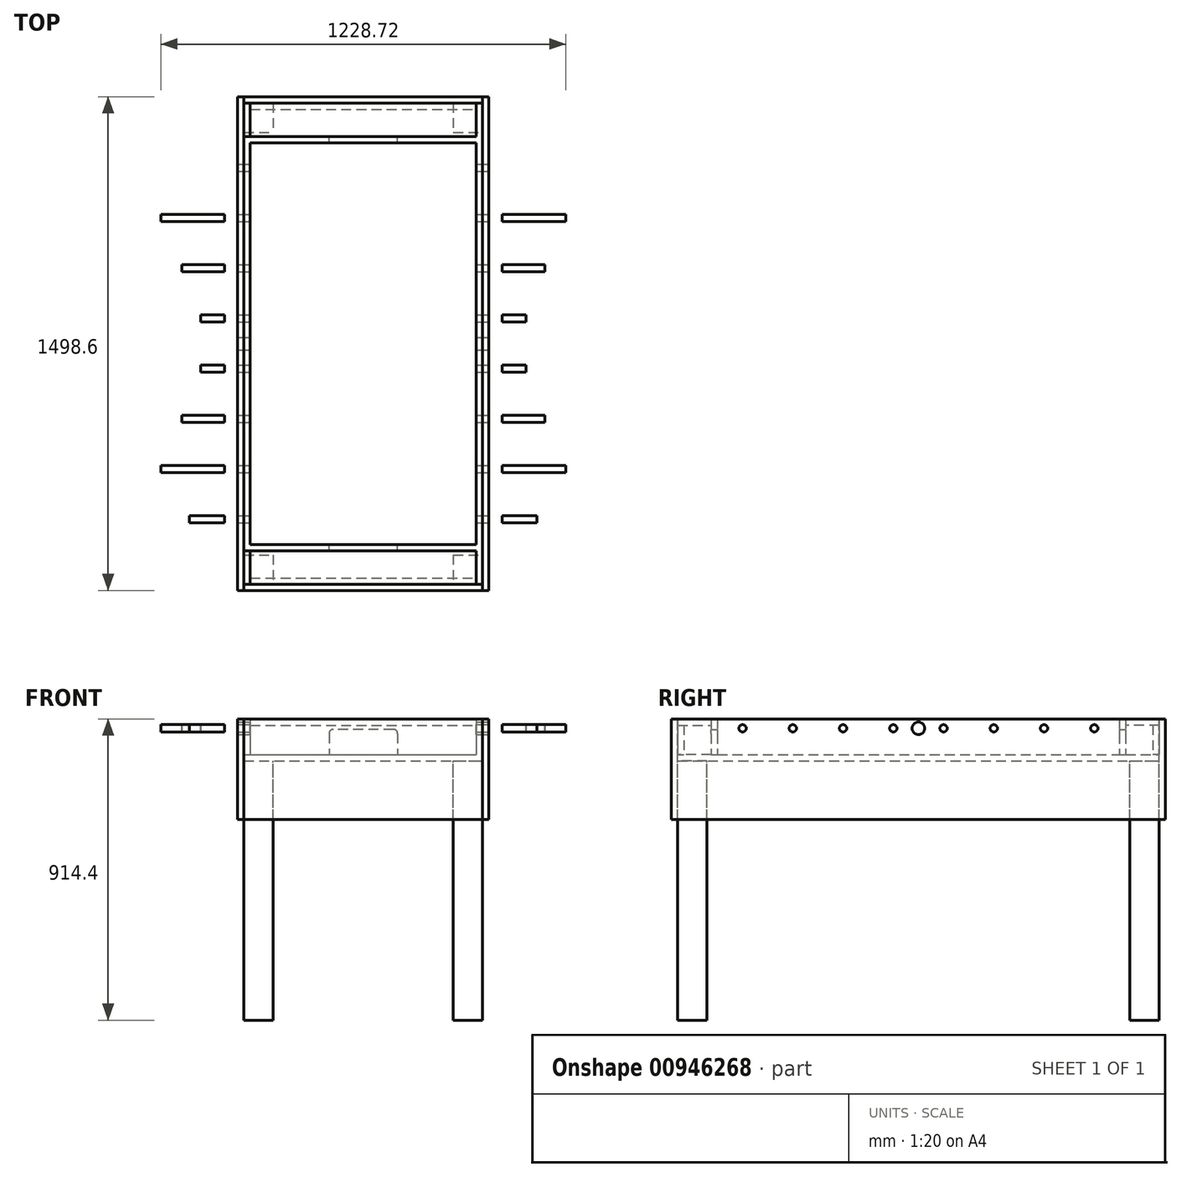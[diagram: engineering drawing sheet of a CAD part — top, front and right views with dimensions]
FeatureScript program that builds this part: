
annotation { "Feature Type Name" : "Feature", "Feature Type Description" : "" }
export const myFeature = defineFeature(function(context is Context, id is Id, definition is map)
    precondition{}
    {
        {
            var Q0;
            Q0=qCreatedBy(makeId("Top.planeOp"),FACE);
            var sketch = newSketch(context, id + "F0", { "sketchPlane" : qUnion([Q0])});
            skLineSegment(sketch, "E0.bottom", {"start": v(-64.22, -45.25) * mm, "end": v(659.68, -45.25) * mm});
            skLineSegment(sketch, "E0.top", {"start": v(-64.22, 1212.05) * mm, "end": v(659.68, 1212.05) * mm});
            skLineSegment(sketch, "E0.left", {"start": v(-64.22, -45.25) * mm, "end": v(-64.22, 1212.05) * mm});
            skLineSegment(sketch, "E0.right", {"start": v(659.68, -45.25) * mm, "end": v(659.68, 1212.05) * mm});
            skSolve(sketch);
        }
        {
            var Q0;
            Q0=makeQuery(id+"F0.imprint","IMPRINT",FACE,{"disambiguationData":[TD([[makeQuery(id+"F0.imprint","IMPRINT",EDGE,{"derivedFrom":sQuery(id+"F0.wireOp",EDGE,"E0.bottom")}),1.0]])]});
            extrude(context, id + "F1", {"entities" : qUnion([Q0]), "oppositeDirection" : true, "depth" : 19.05 * mm, "offsetDistance" : 25.4 * mm});
        }
        {
            var Q0;
            Q0=makeQuery(id+"F1.opExtrude","CAP_FACE",FACE,{"disambiguationData":[OSD([sQuery(id+"F0.wireOp",EDGE,"E0.bottom"),sQuery(id+"F0.wireOp",EDGE,"E0.top"),sQuery(id+"F0.wireOp",EDGE,"E0.left"),sQuery(id+"F0.wireOp",EDGE,"E0.right")])],"isStart":true});
            var sketch = newSketch(context, id + "F2", { "sketchPlane" : qUnion([Q0])});
            skLineSegment(sketch, "E1.bottom", {"start": v(-64.22, -45.25) * mm, "end": v(-45.17, -45.25) * mm});
            skLineSegment(sketch, "E1.top", {"start": v(-64.22, 1212.05) * mm, "end": v(-45.17, 1212.05) * mm});
            skLineSegment(sketch, "E1.left", {"start": v(-64.22, -45.25) * mm, "end": v(-64.22, 1212.05) * mm});
            skLineSegment(sketch, "E1.right", {"start": v(-45.17, -45.25) * mm, "end": v(-45.17, 1212.05) * mm});
            skLineSegment(sketch, "E2.bottom", {"start": v(659.68, -45.25) * mm, "end": v(640.63, -45.25) * mm});
            skLineSegment(sketch, "E2.top", {"start": v(659.68, 1212.05) * mm, "end": v(640.63, 1212.05) * mm});
            skLineSegment(sketch, "E2.left", {"start": v(659.68, -45.25) * mm, "end": v(659.68, 1212.05) * mm});
            skLineSegment(sketch, "E2.right", {"start": v(640.63, -45.25) * mm, "end": v(640.63, 1212.05) * mm});
            skLineSegment(sketch, "E3.bottom", {"start": v(-45.17, -45.25) * mm, "end": v(640.63, -45.25) * mm});
            skLineSegment(sketch, "E3.top", {"start": v(-45.17, -26.2) * mm, "end": v(640.63, -26.2) * mm});
            skLineSegment(sketch, "E3.left", {"start": v(-45.17, -45.25) * mm, "end": v(-45.17, -26.2) * mm});
            skLineSegment(sketch, "E3.right", {"start": v(640.63, -45.25) * mm, "end": v(640.63, -26.2) * mm});
            skLineSegment(sketch, "E4.bottom", {"start": v(-45.17, 1212.05) * mm, "end": v(640.63, 1212.05) * mm});
            skLineSegment(sketch, "E4.top", {"start": v(-45.17, 1193) * mm, "end": v(640.63, 1193) * mm});
            skLineSegment(sketch, "E4.left", {"start": v(-45.17, 1212.05) * mm, "end": v(-45.17, 1193) * mm});
            skLineSegment(sketch, "E4.right", {"start": v(640.63, 1212.05) * mm, "end": v(640.63, 1193) * mm});
            skSolve(sketch);
        }
        {
            var Q0;
            Q0=makeQuery(id+"F2.imprint","IMPRINT",FACE,{"disambiguationData":[TD([[makeQuery(id+"F2.imprint","IMPRINT",EDGE,{"derivedFrom":sQuery(id+"F2.wireOp",EDGE,"E2.bottom")}),1.0]])]});
            extrude(context, id + "F3", {"entities" : qUnion([Q0]), "depth" : 107.95 * mm, "offsetDistance" : 25.4 * mm});
        }
        {
            var Q0;
            Q0=makeQuery(id+"F2.imprint","IMPRINT",FACE,{"disambiguationData":[TD([[makeQuery(id+"F2.imprint","IMPRINT",EDGE,{"derivedFrom":sQuery(id+"F2.wireOp",EDGE,"E1.bottom")}),1.0]])]});
            extrude(context, id + "F4", {"entities" : qUnion([Q0]), "depth" : 107.95 * mm, "offsetDistance" : 25.4 * mm});
        }
        {
            var Q0;
            Q0=makeQuery(id+"F2.imprint","IMPRINT",FACE,{"disambiguationData":[TD([[makeQuery(id+"F2.imprint","IMPRINT",EDGE,{"derivedFrom":sQuery(id+"F2.wireOp",EDGE,"E3.bottom")}),1.0]])]});
            extrude(context, id + "F5", {"entities" : qUnion([Q0]), "depth" : 107.95 * mm, "offsetDistance" : 25.4 * mm});
        }
        {
            var Q0;
            Q0=makeQuery(id+"F2.imprint","IMPRINT",FACE,{"disambiguationData":[TD([[makeQuery(id+"F2.imprint","IMPRINT",EDGE,{"derivedFrom":sQuery(id+"F2.wireOp",EDGE,"E4.bottom")}),-1.0]])]});
            extrude(context, id + "F6", {"entities" : qUnion([Q0]), "depth" : 107.95 * mm, "offsetDistance" : 25.4 * mm});
        }
        {
            var Q0;
            Q0=makeQuery(id+"F3.opExtrude","SWEPT_FACE",FACE,{"disambiguationData":[OSD([sQuery(id+"F2.wireOp",EDGE,"E2.left")])]});
            cPlane(context, id + "F7", {"entities" : qUnion([Q0]), "cplaneType" : CPlaneType.OFFSET, "offset" : 361.95 * mm, "oppositeDirection" : true, "width" : 152.4 * mm, "height" : 152.4 * mm});
        }
        {
            var Q0;
            Q0=qCreatedBy(id+"F7.planeOp",FACE);
            var sketch = newSketch(context, id + "F8", { "sketchPlane" : qUnion([Q0])});
            skLineSegment(sketch, "E5", {"start": v(583.4, 0) * mm, "end": v(583.4, 79.38) * mm});
            skLineSegment(sketch, "E6", {"start": v(583.4, 79.37) * mm, "end": v(507.2, 79.37) * mm});
            skLineSegment(sketch, "E7", {"start": v(507.2, 79.37) * mm, "end": v(354.8, 79.37) * mm});
            skLineSegment(sketch, "E8", {"start": v(354.8, 79.37) * mm, "end": v(202.4, 79.37) * mm});
            skLineSegment(sketch, "E9", {"start": v(202.4, 79.37) * mm, "end": v(50, 79.37) * mm});
            skLineSegment(sketch, "E10", {"start": v(583.4, 79.38) * mm, "end": v(659.6, 79.38) * mm});
            skLineSegment(sketch, "E11", {"start": v(659.6, 79.38) * mm, "end": v(812, 79.38) * mm});
            skLineSegment(sketch, "E12", {"start": v(812, 79.38) * mm, "end": v(964.4, 79.38) * mm});
            skLineSegment(sketch, "E13", {"start": v(964.4, 79.38) * mm, "end": v(1116.8, 79.38) * mm});
            skCircle(sketch, "E14", {"center": v(507.2, 79.37) * mm, "radius": 11.11 * mm});
            skCircle(sketch, "E15", {"center": v(354.8, 79.37) * mm, "radius": 11.11 * mm});
            skCircle(sketch, "E16", {"center": v(202.4, 79.37) * mm, "radius": 11.11 * mm});
            skCircle(sketch, "E17", {"center": v(50, 79.37) * mm, "radius": 11.11 * mm});
            skCircle(sketch, "E18.MirrorC", {"center": v(659.6, 79.37) * mm, "radius": 11.11 * mm});
            skCircle(sketch, "E19.MirrorC", {"center": v(812, 79.37) * mm, "radius": 11.11 * mm});
            skCircle(sketch, "E20.MirrorC", {"center": v(964.4, 79.37) * mm, "radius": 11.11 * mm});
            skCircle(sketch, "E21.MirrorC", {"center": v(1116.8, 79.37) * mm, "radius": 11.11 * mm});
            skCircle(sketch, "E22", {"center": v(583.4, 79.38) * mm, "radius": 19.05 * mm});
            skPoint(sketch, "E23.0", {"position": v(583.4, 0) * mm});
            skSolve(sketch);
        }
        {
            var Q0;
            Q0=makeQuery(id+"F6.opExtrude","SWEPT_FACE",FACE,{"disambiguationData":[OSD([sQuery(id+"F2.wireOp",EDGE,"E4.bottom")])]});
            var sketch = newSketch(context, id + "F9", { "sketchPlane" : qUnion([Q0])});
            skLineSegment(sketch, "E24", {"start": v(-297.73, 0) * mm, "end": v(-297.73, 76.2) * mm});
            skLineSegment(sketch, "E25", {"start": v(-297.73, 76.2) * mm, "end": v(-206.45, 76.2) * mm});
            skLineSegment(sketch, "E26", {"start": v(-297.73, 76.2) * mm, "end": v(-401.71, 76.2) * mm});
            skLineSegment(sketch, "E27.bottom", {"start": v(-389.01, 76.2) * mm, "end": v(-193.75, 76.2) * mm});
            skLineSegment(sketch, "E27.top", {"start": v(-401.71, 0) * mm, "end": v(-193.75, 0) * mm});
            skLineSegment(sketch, "E27.left", {"start": v(-401.71, 63.5) * mm, "end": v(-401.71, 0) * mm});
            skLineSegment(sketch, "E27.right", {"start": v(-193.75, 63.5) * mm, "end": v(-193.75, 0) * mm});
            skPoint(sketch, "E28.visualSharp", {"position": v(-401.71, 76.2) * mm});
            skArc(sketch, "E28.filletArc", {"start": v(-389.01, 76.2) * mm, "mid": v(-398, 72.48) * mm, "end": v(-401.71, 63.5) * mm});
            skPoint(sketch, "E29.visualSharp", {"position": v(-193.75, 76.2) * mm});
            skArc(sketch, "E29.filletArc", {"start": v(-193.75, 63.5) * mm, "mid": v(-197.47, 72.48) * mm, "end": v(-206.45, 76.2) * mm});
            skPoint(sketch, "E30.0", {"position": v(-297.73, 0) * mm});
            skSolve(sketch);
        }
        {
            var Q0;
            Q0 = qSketchRegion(id + "F9", true);
            extrude(context, id + "F10", {"entities" : qUnion([Q0]), "operationType" : NewBodyOperationType.REMOVE, "endBound" : BoundingType.THROUGH_ALL, "oppositeDirection" : true, "depth" : 25.4 * mm, "offsetDistance" : 25.4 * mm});
        }
        {
            var Q0;
            Q0=makeQuery(id+"F8.imprint","IMPRINT",FACE,{"disambiguationData":[TD([[makeQuery(id+"F8.imprint","IMPRINT",EDGE,{"derivedFrom":sQuery(id+"F8.wireOp",EDGE,"E21.MirrorC")}),-1.0]])]});
            var Q1;
            Q1=makeQuery(id+"F8.imprint","IMPRINT",FACE,{"disambiguationData":[TD([[makeQuery(id+"F8.imprint","IMPRINT",EDGE,{"derivedFrom":sQuery(id+"F8.wireOp",EDGE,"E17")}),1.0]])]});
            extrude(context, id + "F11", {"entities" : qUnion([Q0, Q1]), "depth" : 1054.1 * mm, "offsetDistance" : 25.4 * mm, "symmetric" : true});
        }
        {
            var Q0;
            {var subQ0=sQuery(id+"F8.wireOp",EDGE,"E13");var subQ1=sQuery(id+"F8.wireOp",EDGE,"E12");var subQ2=makeQuery(id+"F8.imprint","INTERSECT",VERTEX,{"derivedFrom":[subQ1,subQ0]});Q0=makeQuery(id+"F8.imprint","IMPRINT",FACE,{"disambiguationData":[TD([[makeQuery(id+"F8.imprint","IMPRINT",EDGE,{"disambiguationData":[TD([[subQ2,1.0]])],"derivedFrom":subQ1}),-1.0]])]});}
            var Q1;
            {var subQ0=sQuery(id+"F8.wireOp",EDGE,"E13");var subQ1=sQuery(id+"F8.wireOp",EDGE,"E12");var subQ2=makeQuery(id+"F8.imprint","INTERSECT",VERTEX,{"derivedFrom":[subQ1,subQ0]});Q1=makeQuery(id+"F8.imprint","IMPRINT",FACE,{"disambiguationData":[TD([[makeQuery(id+"F8.imprint","IMPRINT",EDGE,{"disambiguationData":[TD([[subQ2,1.0]])],"derivedFrom":subQ1}),1.0]])]});}
            var Q2;
            {var subQ0=sQuery(id+"F8.wireOp",EDGE,"E9");var subQ1=sQuery(id+"F8.wireOp",EDGE,"E8");var subQ2=makeQuery(id+"F8.imprint","INTERSECT",VERTEX,{"derivedFrom":[subQ1,subQ0]});Q2=makeQuery(id+"F8.imprint","IMPRINT",FACE,{"disambiguationData":[TD([[makeQuery(id+"F8.imprint","IMPRINT",EDGE,{"disambiguationData":[TD([[subQ2,1.0]])],"derivedFrom":subQ1}),1.0]])]});}
            var Q3;
            {var subQ0=sQuery(id+"F8.wireOp",EDGE,"E9");var subQ1=sQuery(id+"F8.wireOp",EDGE,"E8");var subQ2=makeQuery(id+"F8.imprint","INTERSECT",VERTEX,{"derivedFrom":[subQ1,subQ0]});Q3=makeQuery(id+"F8.imprint","IMPRINT",FACE,{"disambiguationData":[TD([[makeQuery(id+"F8.imprint","IMPRINT",EDGE,{"disambiguationData":[TD([[subQ2,1.0]])],"derivedFrom":subQ1}),-1.0]])]});}
            extrude(context, id + "F12", {"entities" : qUnion([Q0, Q1, Q2, Q3]), "depth" : 1228.72 * mm, "offsetDistance" : 25.4 * mm, "symmetric" : true});
        }
        {
            var Q0;
            {var subQ0=sQuery(id+"F8.wireOp",EDGE,"E12");var subQ1=sQuery(id+"F8.wireOp",EDGE,"E11");var subQ2=makeQuery(id+"F8.imprint","INTERSECT",VERTEX,{"derivedFrom":[subQ1,subQ0]});Q0=makeQuery(id+"F8.imprint","IMPRINT",FACE,{"disambiguationData":[TD([[makeQuery(id+"F8.imprint","IMPRINT",EDGE,{"disambiguationData":[TD([[subQ2,1.0]])],"derivedFrom":subQ1}),-1.0]])]});}
            var Q1;
            {var subQ0=sQuery(id+"F8.wireOp",EDGE,"E12");var subQ1=sQuery(id+"F8.wireOp",EDGE,"E11");var subQ2=makeQuery(id+"F8.imprint","INTERSECT",VERTEX,{"derivedFrom":[subQ1,subQ0]});Q1=makeQuery(id+"F8.imprint","IMPRINT",FACE,{"disambiguationData":[TD([[makeQuery(id+"F8.imprint","IMPRINT",EDGE,{"disambiguationData":[TD([[subQ2,1.0]])],"derivedFrom":subQ1}),1.0]])]});}
            var Q2;
            {var subQ0=sQuery(id+"F8.wireOp",EDGE,"E8");var subQ1=sQuery(id+"F8.wireOp",EDGE,"E7");var subQ2=makeQuery(id+"F8.imprint","INTERSECT",VERTEX,{"derivedFrom":[subQ1,subQ0]});Q2=makeQuery(id+"F8.imprint","IMPRINT",FACE,{"disambiguationData":[TD([[makeQuery(id+"F8.imprint","IMPRINT",EDGE,{"disambiguationData":[TD([[subQ2,1.0]])],"derivedFrom":subQ1}),-1.0]])]});}
            var Q3;
            {var subQ0=sQuery(id+"F8.wireOp",EDGE,"E8");var subQ1=sQuery(id+"F8.wireOp",EDGE,"E7");var subQ2=makeQuery(id+"F8.imprint","INTERSECT",VERTEX,{"derivedFrom":[subQ1,subQ0]});Q3=makeQuery(id+"F8.imprint","IMPRINT",FACE,{"disambiguationData":[TD([[makeQuery(id+"F8.imprint","IMPRINT",EDGE,{"disambiguationData":[TD([[subQ2,1.0]])],"derivedFrom":subQ1}),1.0]])]});}
            extrude(context, id + "F13", {"entities" : qUnion([Q0, Q1, Q2, Q3]), "depth" : 1101.72 * mm, "offsetDistance" : 25.4 * mm, "symmetric" : true});
        }
        {
            var Q0;
            {var subQ0=sQuery(id+"F8.wireOp",EDGE,"E7");var subQ1=sQuery(id+"F8.wireOp",EDGE,"E6");var subQ2=makeQuery(id+"F8.imprint","INTERSECT",VERTEX,{"derivedFrom":[subQ1,subQ0]});Q0=makeQuery(id+"F8.imprint","IMPRINT",FACE,{"disambiguationData":[TD([[makeQuery(id+"F8.imprint","IMPRINT",EDGE,{"disambiguationData":[TD([[subQ2,1.0]])],"derivedFrom":subQ1}),1.0]])]});}
            var Q1;
            {var subQ0=sQuery(id+"F8.wireOp",EDGE,"E7");var subQ1=sQuery(id+"F8.wireOp",EDGE,"E6");var subQ2=makeQuery(id+"F8.imprint","INTERSECT",VERTEX,{"derivedFrom":[subQ1,subQ0]});Q1=makeQuery(id+"F8.imprint","IMPRINT",FACE,{"disambiguationData":[TD([[makeQuery(id+"F8.imprint","IMPRINT",EDGE,{"disambiguationData":[TD([[subQ2,1.0]])],"derivedFrom":subQ1}),-1.0]])]});}
            var Q2;
            {var subQ0=sQuery(id+"F8.wireOp",EDGE,"E11");var subQ1=sQuery(id+"F8.wireOp",EDGE,"E10");var subQ2=makeQuery(id+"F8.imprint","INTERSECT",VERTEX,{"derivedFrom":[subQ1,subQ0]});Q2=makeQuery(id+"F8.imprint","IMPRINT",FACE,{"disambiguationData":[TD([[makeQuery(id+"F8.imprint","IMPRINT",EDGE,{"disambiguationData":[TD([[subQ2,1.0]])],"derivedFrom":subQ1}),-1.0]])]});}
            var Q3;
            {var subQ0=sQuery(id+"F8.wireOp",EDGE,"E11");var subQ1=sQuery(id+"F8.wireOp",EDGE,"E10");var subQ2=makeQuery(id+"F8.imprint","INTERSECT",VERTEX,{"derivedFrom":[subQ1,subQ0]});Q3=makeQuery(id+"F8.imprint","IMPRINT",FACE,{"disambiguationData":[TD([[makeQuery(id+"F8.imprint","IMPRINT",EDGE,{"disambiguationData":[TD([[subQ2,1.0]])],"derivedFrom":subQ1}),1.0]])]});}
            extrude(context, id + "F14", {"entities" : qUnion([Q0, Q1, Q2, Q3]), "depth" : 987.42 * mm, "offsetDistance" : 25.4 * mm, "symmetric" : true});
        }
        {
            var Q0;
            Q0=makeQuery(id+"F1.opExtrude","CAP_FACE",FACE,{"disambiguationData":[OSD([sQuery(id+"F0.wireOp",EDGE,"E0.bottom"),sQuery(id+"F0.wireOp",EDGE,"E0.top"),sQuery(id+"F0.wireOp",EDGE,"E0.left"),sQuery(id+"F0.wireOp",EDGE,"E0.right")])],"isStart":true});
            var sketch = newSketch(context, id + "F15", { "sketchPlane" : qUnion([Q0])});
            skLineSegment(sketch, "E31.bottom", {"start": v(-64.22, -45.25) * mm, "end": v(659.68, -45.25) * mm});
            skLineSegment(sketch, "E31.top", {"start": v(-64.22, -146.85) * mm, "end": v(659.68, -146.85) * mm});
            skLineSegment(sketch, "E31.left", {"start": v(-64.22, -45.25) * mm, "end": v(-64.22, -146.85) * mm});
            skLineSegment(sketch, "E31.right", {"start": v(659.68, -45.25) * mm, "end": v(659.68, -146.85) * mm});
            skLineSegment(sketch, "E32.bottom", {"start": v(-64.22, 1212.05) * mm, "end": v(659.68, 1212.05) * mm});
            skLineSegment(sketch, "E32.top", {"start": v(-64.22, 1212.05) * mm, "end": v(659.68, 1212.05) * mm});
            skLineSegment(sketch, "E32.left", {"start": v(-64.22, 1212.05) * mm, "end": v(-64.22, 1212.05) * mm});
            skLineSegment(sketch, "E32.right", {"start": v(659.68, 1212.05) * mm, "end": v(659.68, 1212.05) * mm});
            skLineSegment(sketch, "E33.top", {"start": v(-64.22, 1313.65) * mm, "end": v(659.68, 1313.65) * mm});
            skLineSegment(sketch, "E33.left", {"start": v(-64.22, 1212.05) * mm, "end": v(-64.22, 1313.65) * mm});
            skLineSegment(sketch, "E33.right", {"start": v(659.68, 1212.05) * mm, "end": v(659.68, 1313.65) * mm});
            skSolve(sketch);
        }
        {
            var Q0;
            Q0=makeQuery(id+"F15.imprint","IMPRINT",FACE,{"disambiguationData":[TD([[makeQuery(id+"F15.imprint","IMPRINT",EDGE,{"derivedFrom":sQuery(id+"F15.wireOp",EDGE,"E32.bottom")}),1.0]])]});
            var Q1;
            Q1=makeQuery(id+"F15.imprint","IMPRINT",FACE,{"disambiguationData":[TD([[makeQuery(id+"F15.imprint","IMPRINT",EDGE,{"derivedFrom":sQuery(id+"F15.wireOp",EDGE,"E31.bottom")}),-1.0]])]});
            extrude(context, id + "F16", {"entities" : qUnion([Q0, Q1]), "operationType" : NewBodyOperationType.ADD, "oppositeDirection" : true, "depth" : 19.05 * mm, "offsetDistance" : 25.4 * mm});
        }
        {
            var Q0;
            Q0=makeQuery(id+"F16.boolean.opBoolean","MERGE",FACE,{"derivedFrom":[makeQuery(id+"F1.opExtrude","CAP_FACE",FACE,{"disambiguationData":[OSD([sQuery(id+"F0.wireOp",EDGE,"E0.bottom"),sQuery(id+"F0.wireOp",EDGE,"E0.top"),sQuery(id+"F0.wireOp",EDGE,"E0.left"),sQuery(id+"F0.wireOp",EDGE,"E0.right")])],"isStart":true}),makeQuery(id+"F16.opExtrude","CAP_FACE",FACE,{"disambiguationData":[OSD([sQuery(id+"F15.wireOp",EDGE,"E31.bottom"),sQuery(id+"F15.wireOp",EDGE,"E31.top"),sQuery(id+"F15.wireOp",EDGE,"E31.left"),sQuery(id+"F15.wireOp",EDGE,"E31.right")])],"isStart":true}),makeQuery(id+"F16.opExtrude","CAP_FACE",FACE,{"disambiguationData":[OSD([sQuery(id+"F15.wireOp",EDGE,"E32.bottom"),sQuery(id+"F15.wireOp",EDGE,"E33.top"),sQuery(id+"F15.wireOp",EDGE,"E33.left"),sQuery(id+"F15.wireOp",EDGE,"E33.right")])],"isStart":true})]});
            var sketch = newSketch(context, id + "F17", { "sketchPlane" : qUnion([Q0])});
            skPoint(sketch, "E34.0", {"position": v(-45.17, 1212.05) * mm});
            skPoint(sketch, "E35.0", {"position": v(640.63, 1212.05) * mm});
            skPoint(sketch, "E36.0", {"position": v(640.63, -45.25) * mm});
            skPoint(sketch, "E37.0", {"position": v(-45.17, -45.25) * mm});
            skLineSegment(sketch, "E38.bottom", {"start": v(-45.17, -45.25) * mm, "end": v(-64.22, -45.25) * mm});
            skLineSegment(sketch, "E38.top", {"start": v(-45.17, -146.85) * mm, "end": v(-64.22, -146.85) * mm});
            skLineSegment(sketch, "E38.left", {"start": v(-45.17, -45.25) * mm, "end": v(-45.17, -146.85) * mm});
            skLineSegment(sketch, "E38.right", {"start": v(-64.22, -45.25) * mm, "end": v(-64.22, -146.85) * mm});
            skLineSegment(sketch, "E39.bottom", {"start": v(640.63, -45.25) * mm, "end": v(659.68, -45.25) * mm});
            skLineSegment(sketch, "E39.top", {"start": v(640.63, -146.85) * mm, "end": v(659.68, -146.85) * mm});
            skLineSegment(sketch, "E39.left", {"start": v(640.63, -45.25) * mm, "end": v(640.63, -146.85) * mm});
            skLineSegment(sketch, "E39.right", {"start": v(659.68, -45.25) * mm, "end": v(659.68, -146.85) * mm});
            skLineSegment(sketch, "E40.bottom", {"start": v(-45.17, 1212.05) * mm, "end": v(-64.22, 1212.05) * mm});
            skLineSegment(sketch, "E40.top", {"start": v(-45.17, 1313.65) * mm, "end": v(-64.22, 1313.65) * mm});
            skLineSegment(sketch, "E40.left", {"start": v(-45.17, 1212.05) * mm, "end": v(-45.17, 1313.65) * mm});
            skLineSegment(sketch, "E40.right", {"start": v(-64.22, 1212.05) * mm, "end": v(-64.22, 1313.65) * mm});
            skLineSegment(sketch, "E41.bottom", {"start": v(640.63, 1212.05) * mm, "end": v(659.68, 1212.05) * mm});
            skLineSegment(sketch, "E41.top", {"start": v(640.63, 1313.65) * mm, "end": v(659.68, 1313.65) * mm});
            skLineSegment(sketch, "E41.left", {"start": v(640.63, 1212.05) * mm, "end": v(640.63, 1313.65) * mm});
            skLineSegment(sketch, "E41.right", {"start": v(659.68, 1212.05) * mm, "end": v(659.68, 1313.65) * mm});
            skSolve(sketch);
        }
        {
            var Q0;
            Q0=makeQuery(id+"F17.imprint","IMPRINT",FACE,{"disambiguationData":[TD([[makeQuery(id+"F17.imprint","IMPRINT",EDGE,{"derivedFrom":sQuery(id+"F17.wireOp",EDGE,"E41.bottom")}),1.0]])]});
            var Q1;
            Q1=makeQuery(id+"F17.imprint","IMPRINT",FACE,{"disambiguationData":[TD([[makeQuery(id+"F17.imprint","IMPRINT",EDGE,{"derivedFrom":sQuery(id+"F17.wireOp",EDGE,"E40.bottom")}),-1.0]])]});
            var Q2;
            Q2=makeQuery(id+"F17.imprint","IMPRINT",FACE,{"disambiguationData":[TD([[makeQuery(id+"F17.imprint","IMPRINT",EDGE,{"derivedFrom":sQuery(id+"F17.wireOp",EDGE,"E39.bottom")}),-1.0]])]});
            var Q3;
            Q3=makeQuery(id+"F17.imprint","IMPRINT",FACE,{"disambiguationData":[TD([[makeQuery(id+"F17.imprint","IMPRINT",EDGE,{"derivedFrom":sQuery(id+"F17.wireOp",EDGE,"E38.bottom")}),1.0]])]});
            var Q4;
            Q4=makeQuery(id+"F4.opExtrude","CAP_FACE",FACE,{"disambiguationData":[OSD([sQuery(id+"F2.wireOp",EDGE,"E1.bottom"),sQuery(id+"F2.wireOp",EDGE,"E1.top"),sQuery(id+"F2.wireOp",EDGE,"E1.left"),sQuery(id+"F2.wireOp",EDGE,"E1.right"),sQuery(id+"F2.wireOp",EDGE,"E3.left"),sQuery(id+"F2.wireOp",EDGE,"E4.left")])],"isStart":false});
            extrude(context, id + "F18", {"entities" : qUnion([Q0, Q1, Q2, Q3]), "operationType" : NewBodyOperationType.ADD, "endBound" : BoundingType.UP_TO_SURFACE, "depth" : 63.5 * mm, "endBoundEntityFace" : qUnion([Q4]), "offsetDistance" : 25.4 * mm});
        }
        {
            var Q0;
            Q0=makeQuery(id+"F16.boolean.opBoolean","MERGE",FACE,{"derivedFrom":[makeQuery(id+"F1.opExtrude","CAP_FACE",FACE,{"disambiguationData":[OSD([sQuery(id+"F0.wireOp",EDGE,"E0.bottom"),sQuery(id+"F0.wireOp",EDGE,"E0.top"),sQuery(id+"F0.wireOp",EDGE,"E0.left"),sQuery(id+"F0.wireOp",EDGE,"E0.right")])],"isStart":true}),makeQuery(id+"F16.opExtrude","CAP_FACE",FACE,{"disambiguationData":[OSD([sQuery(id+"F15.wireOp",EDGE,"E31.bottom"),sQuery(id+"F15.wireOp",EDGE,"E31.top"),sQuery(id+"F15.wireOp",EDGE,"E31.left"),sQuery(id+"F15.wireOp",EDGE,"E31.right")])],"isStart":true}),makeQuery(id+"F16.opExtrude","CAP_FACE",FACE,{"disambiguationData":[OSD([sQuery(id+"F15.wireOp",EDGE,"E32.bottom"),sQuery(id+"F15.wireOp",EDGE,"E33.top"),sQuery(id+"F15.wireOp",EDGE,"E33.left"),sQuery(id+"F15.wireOp",EDGE,"E33.right")])],"isStart":true})]});
            var sketch = newSketch(context, id + "F19", { "sketchPlane" : qUnion([Q0])});
            skPoint(sketch, "E42.0", {"position": v(-45.17, -146.85) * mm});
            skPoint(sketch, "E43.0", {"position": v(-45.17, 1313.65) * mm});
            skLineSegment(sketch, "E44.0", {"start": v(640.63, -146.85) * mm, "end": v(640.63, 1313.65) * mm});
            skLineSegment(sketch, "E45.bottom", {"start": v(-45.17, -146.85) * mm, "end": v(640.63, -146.85) * mm});
            skLineSegment(sketch, "E45.top", {"start": v(-45.17, -127.8) * mm, "end": v(640.63, -127.8) * mm});
            skLineSegment(sketch, "E45.left", {"start": v(-45.17, -146.85) * mm, "end": v(-45.17, -127.8) * mm});
            skLineSegment(sketch, "E45.right", {"start": v(640.63, -146.85) * mm, "end": v(640.63, -127.8) * mm});
            skLineSegment(sketch, "E46.bottom", {"start": v(-45.17, 1313.65) * mm, "end": v(640.63, 1313.65) * mm});
            skLineSegment(sketch, "E46.top", {"start": v(-45.17, 1294.6) * mm, "end": v(640.63, 1294.6) * mm});
            skLineSegment(sketch, "E46.left", {"start": v(-45.17, 1313.65) * mm, "end": v(-45.17, 1294.6) * mm});
            skLineSegment(sketch, "E46.right", {"start": v(640.63, 1313.65) * mm, "end": v(640.63, 1294.6) * mm});
            skSolve(sketch);
        }
        {
            var Q0;
            Q0=makeQuery(id+"F19.imprint","IMPRINT",FACE,{"disambiguationData":[TD([[makeQuery(id+"F19.imprint","IMPRINT",EDGE,{"derivedFrom":sQuery(id+"F19.wireOp",EDGE,"E45.bottom")}),1.0]])]});
            var Q1;
            Q1=makeQuery(id+"F19.imprint","IMPRINT",FACE,{"disambiguationData":[TD([[makeQuery(id+"F19.imprint","IMPRINT",EDGE,{"derivedFrom":sQuery(id+"F19.wireOp",EDGE,"E46.bottom")}),-1.0]])]});
            var Q2;
            Q2=makeQuery(id+"F18.boolean.opBoolean","MERGE",FACE,{"derivedFrom":[makeQuery(id+"F4.opExtrude","CAP_FACE",FACE,{"disambiguationData":[OSD([sQuery(id+"F2.wireOp",EDGE,"E1.bottom"),sQuery(id+"F2.wireOp",EDGE,"E1.top"),sQuery(id+"F2.wireOp",EDGE,"E1.left"),sQuery(id+"F2.wireOp",EDGE,"E1.right"),sQuery(id+"F2.wireOp",EDGE,"E3.left"),sQuery(id+"F2.wireOp",EDGE,"E4.left")])],"isStart":false}),makeQuery(id+"F18.opExtrude","CAP_FACE",FACE,{"disambiguationData":[OSD([sQuery(id+"F17.wireOp",EDGE,"E38.bottom"),sQuery(id+"F17.wireOp",EDGE,"E38.top"),sQuery(id+"F17.wireOp",EDGE,"E38.left"),sQuery(id+"F17.wireOp",EDGE,"E38.right")])],"isStart":false}),makeQuery(id+"F18.opExtrude","CAP_FACE",FACE,{"disambiguationData":[OSD([sQuery(id+"F17.wireOp",EDGE,"E40.bottom"),sQuery(id+"F17.wireOp",EDGE,"E40.top"),sQuery(id+"F17.wireOp",EDGE,"E40.left"),sQuery(id+"F17.wireOp",EDGE,"E40.right")])],"isStart":false})]});
            extrude(context, id + "F20", {"entities" : qUnion([Q0, Q1]), "depth" : 88.9 * mm, "endBoundEntityFace" : qUnion([Q2]), "offsetDistance" : 25.4 * mm});
        }
        {
            var Q0;
            Q0=makeQuery(id+"F16.boolean.opBoolean","MERGE",FACE,{"derivedFrom":[makeQuery(id+"F1.opExtrude","CAP_FACE",FACE,{"disambiguationData":[OSD([sQuery(id+"F0.wireOp",EDGE,"E0.bottom"),sQuery(id+"F0.wireOp",EDGE,"E0.top"),sQuery(id+"F0.wireOp",EDGE,"E0.left"),sQuery(id+"F0.wireOp",EDGE,"E0.right")])],"isStart":false}),makeQuery(id+"F16.opExtrude","CAP_FACE",FACE,{"disambiguationData":[OSD([sQuery(id+"F15.wireOp",EDGE,"E31.bottom"),sQuery(id+"F15.wireOp",EDGE,"E31.top"),sQuery(id+"F15.wireOp",EDGE,"E31.left"),sQuery(id+"F15.wireOp",EDGE,"E31.right")])],"isStart":false}),makeQuery(id+"F16.opExtrude","CAP_FACE",FACE,{"disambiguationData":[OSD([sQuery(id+"F15.wireOp",EDGE,"E32.bottom"),sQuery(id+"F15.wireOp",EDGE,"E33.top"),sQuery(id+"F15.wireOp",EDGE,"E33.left"),sQuery(id+"F15.wireOp",EDGE,"E33.right")])],"isStart":false})]});
            var sketch = newSketch(context, id + "F21", { "sketchPlane" : qUnion([Q0])});
            skLineSegment(sketch, "E47.bottom", {"start": v(-64.22, -1313.65) * mm, "end": v(24.68, -1313.65) * mm});
            skLineSegment(sketch, "E47.top", {"start": v(-64.22, -1224.75) * mm, "end": v(24.68, -1224.75) * mm});
            skLineSegment(sketch, "E47.left", {"start": v(-64.22, -1313.65) * mm, "end": v(-64.22, -1224.75) * mm});
            skLineSegment(sketch, "E47.right", {"start": v(24.68, -1313.65) * mm, "end": v(24.68, -1224.75) * mm});
            skLineSegment(sketch, "E48.0.1.0", {"start": v(-64.22, 146.85) * mm, "end": v(24.68, 146.85) * mm});
            skLineSegment(sketch, "E48.0.1.1", {"start": v(-64.22, 57.95) * mm, "end": v(-64.22, 146.85) * mm});
            skLineSegment(sketch, "E48.0.1.2", {"start": v(24.68, 57.95) * mm, "end": v(24.68, 146.85) * mm});
            skLineSegment(sketch, "E48.0.1.3", {"start": v(-64.22, 57.95) * mm, "end": v(24.68, 57.95) * mm});
            skLineSegment(sketch, "E48.1.0.0", {"start": v(570.78, -1224.75) * mm, "end": v(659.68, -1224.75) * mm});
            skLineSegment(sketch, "E48.1.0.1", {"start": v(570.78, -1313.65) * mm, "end": v(570.78, -1224.75) * mm});
            skLineSegment(sketch, "E48.1.0.2", {"start": v(659.68, -1313.65) * mm, "end": v(659.68, -1224.75) * mm});
            skLineSegment(sketch, "E48.1.0.3", {"start": v(570.78, -1313.65) * mm, "end": v(659.68, -1313.65) * mm});
            skLineSegment(sketch, "E48.1.1.0", {"start": v(570.78, 146.85) * mm, "end": v(659.68, 146.85) * mm});
            skLineSegment(sketch, "E48.1.1.1", {"start": v(570.78, 57.95) * mm, "end": v(570.78, 146.85) * mm});
            skLineSegment(sketch, "E48.1.1.2", {"start": v(659.68, 57.95) * mm, "end": v(659.68, 146.85) * mm});
            skLineSegment(sketch, "E48.1.1.3", {"start": v(570.78, 57.95) * mm, "end": v(659.68, 57.95) * mm});
            skLineSegment(sketch, "E48.direction1", {"start": v(-64.22, -1313.65) * mm, "end": v(570.78, -1313.65) * mm, "construction": true});
            skLineSegment(sketch, "E48.direction2", {"start": v(-64.22, -1313.65) * mm, "end": v(-64.22, 57.95) * mm, "construction": true});
            skSolve(sketch);
        }
        {
            var Q0;
            Q0 = qSketchRegion(id + "F21", true);
            extrude(context, id + "F22", {"entities" : qUnion([Q0]), "depth" : 787.4 * mm, "offsetDistance" : 25.4 * mm});
        }
        {
            var Q0;
            Q0=makeQuery(id+"F20.opExtrude","CAP_FACE",FACE,{"disambiguationData":[OSD([sQuery(id+"F19.wireOp",EDGE,"E45.bottom"),sQuery(id+"F19.wireOp",EDGE,"E45.top"),sQuery(id+"F19.wireOp",EDGE,"E45.left"),sQuery(id+"F19.wireOp",EDGE,"E45.right")])],"isStart":false});
            var sketch = newSketch(context, id + "F23", { "sketchPlane" : qUnion([Q0])});
            skLineSegment(sketch, "E49.0", {"start": v(-45.17, -45.25) * mm, "end": v(640.63, -45.25) * mm});
            skLineSegment(sketch, "E50.0", {"start": v(-45.17, 1212.05) * mm, "end": v(640.63, 1212.05) * mm});
            skLineSegment(sketch, "E51.bottom", {"start": v(640.63, -146.85) * mm, "end": v(-45.17, -146.85) * mm});
            skLineSegment(sketch, "E51.top", {"start": v(640.63, -45.25) * mm, "end": v(-45.17, -45.25) * mm});
            skLineSegment(sketch, "E51.left", {"start": v(640.63, -146.85) * mm, "end": v(640.63, -45.25) * mm});
            skLineSegment(sketch, "E51.right", {"start": v(-45.17, -146.85) * mm, "end": v(-45.17, -45.25) * mm});
            skLineSegment(sketch, "E52.0", {"start": v(-45.17, 1313.65) * mm, "end": v(640.63, 1313.65) * mm});
            skLineSegment(sketch, "E53.bottom", {"start": v(640.63, 1313.65) * mm, "end": v(-45.17, 1313.65) * mm});
            skLineSegment(sketch, "E53.top", {"start": v(640.63, 1212.05) * mm, "end": v(-45.17, 1212.05) * mm});
            skLineSegment(sketch, "E53.left", {"start": v(640.63, 1313.65) * mm, "end": v(640.63, 1212.05) * mm});
            skLineSegment(sketch, "E53.right", {"start": v(-45.17, 1313.65) * mm, "end": v(-45.17, 1212.05) * mm});
            skSolve(sketch);
        }
        {
            var Q0;
            Q0 = qSketchRegion(id + "F23", true);
            extrude(context, id + "F24", {"entities" : qUnion([Q0]), "depth" : 19.05 * mm, "offsetDistance" : 25.4 * mm});
        }
        {
            var Q0;
            Q0=makeQuery(id+"F18.boolean.opBoolean","MERGE",FACE,{"derivedFrom":[makeQuery(id+"F4.opExtrude","CAP_FACE",FACE,{"disambiguationData":[OSD([sQuery(id+"F2.wireOp",EDGE,"E1.bottom"),sQuery(id+"F2.wireOp",EDGE,"E1.top"),sQuery(id+"F2.wireOp",EDGE,"E1.left"),sQuery(id+"F2.wireOp",EDGE,"E1.right"),sQuery(id+"F2.wireOp",EDGE,"E3.left"),sQuery(id+"F2.wireOp",EDGE,"E4.left")])],"isStart":false}),makeQuery(id+"F18.opExtrude","CAP_FACE",FACE,{"disambiguationData":[OSD([sQuery(id+"F17.wireOp",EDGE,"E38.bottom"),sQuery(id+"F17.wireOp",EDGE,"E38.top"),sQuery(id+"F17.wireOp",EDGE,"E38.left"),sQuery(id+"F17.wireOp",EDGE,"E38.right")])],"isStart":false}),makeQuery(id+"F18.opExtrude","CAP_FACE",FACE,{"disambiguationData":[OSD([sQuery(id+"F17.wireOp",EDGE,"E40.bottom"),sQuery(id+"F17.wireOp",EDGE,"E40.top"),sQuery(id+"F17.wireOp",EDGE,"E40.left"),sQuery(id+"F17.wireOp",EDGE,"E40.right")])],"isStart":false})]});
            var sketch = newSketch(context, id + "F25", { "sketchPlane" : qUnion([Q0])});
            skLineSegment(sketch, "E54.0", {"start": v(659.68, -146.85) * mm, "end": v(659.68, 1313.65) * mm});
            skLineSegment(sketch, "E55.0", {"start": v(640.63, 1313.65) * mm, "end": v(-45.17, 1313.65) * mm});
            skLineSegment(sketch, "E56.0", {"start": v(-45.17, -146.85) * mm, "end": v(640.63, -146.85) * mm});
            skLineSegment(sketch, "E57.0", {"start": v(-64.22, -146.85) * mm, "end": v(-64.22, 1313.65) * mm});
            skLineSegment(sketch, "E58.bottom", {"start": v(-64.22, -146.85) * mm, "end": v(659.68, -146.85) * mm});
            skLineSegment(sketch, "E58.top", {"start": v(-64.22, -146.85) * mm, "end": v(659.68, -146.85) * mm});
            skLineSegment(sketch, "E58.left", {"start": v(-64.22, -146.85) * mm, "end": v(-64.22, -146.85) * mm});
            skLineSegment(sketch, "E58.right", {"start": v(659.68, -146.85) * mm, "end": v(659.68, -146.85) * mm});
            skLineSegment(sketch, "E59.top", {"start": v(-64.22, -165.9) * mm, "end": v(659.68, -165.9) * mm});
            skLineSegment(sketch, "E59.left", {"start": v(-64.22, -146.85) * mm, "end": v(-64.22, -165.9) * mm});
            skLineSegment(sketch, "E59.right", {"start": v(659.68, -146.85) * mm, "end": v(659.68, -165.9) * mm});
            skLineSegment(sketch, "E60.bottom", {"start": v(-64.22, 1313.65) * mm, "end": v(659.68, 1313.65) * mm});
            skLineSegment(sketch, "E60.top", {"start": v(-64.22, 1332.7) * mm, "end": v(659.68, 1332.7) * mm});
            skLineSegment(sketch, "E60.left", {"start": v(-64.22, 1313.65) * mm, "end": v(-64.22, 1332.7) * mm});
            skLineSegment(sketch, "E60.right", {"start": v(659.68, 1313.65) * mm, "end": v(659.68, 1332.7) * mm});
            skLineSegment(sketch, "E61.bottom", {"start": v(-64.22, -165.9) * mm, "end": v(-83.27, -165.9) * mm});
            skLineSegment(sketch, "E61.top", {"start": v(-64.22, 1332.7) * mm, "end": v(-83.27, 1332.7) * mm});
            skLineSegment(sketch, "E61.left", {"start": v(-64.22, -165.9) * mm, "end": v(-64.22, 1332.7) * mm});
            skLineSegment(sketch, "E61.right", {"start": v(-83.27, -165.9) * mm, "end": v(-83.27, 1332.7) * mm});
            skLineSegment(sketch, "E62.bottom", {"start": v(659.68, -165.9) * mm, "end": v(678.73, -165.9) * mm});
            skLineSegment(sketch, "E62.top", {"start": v(659.68, 1332.7) * mm, "end": v(678.73, 1332.7) * mm});
            skLineSegment(sketch, "E62.left", {"start": v(659.68, -165.9) * mm, "end": v(659.68, 1332.7) * mm});
            skLineSegment(sketch, "E62.right", {"start": v(678.73, -165.9) * mm, "end": v(678.73, 1332.7) * mm});
            skSolve(sketch);
        }
        {
            var Q0;
            {var subQ0=sQuery(id+"F25.wireOp",EDGE,"E59.top");Q0=makeQuery(id+"F25.imprint","IMPRINT",FACE,{"disambiguationData":[TD([[makeQuery(id+"F25.imprint","IMPRINT",EDGE,{"derivedFrom":subQ0}),1.0]])]});}
            var Q1;
            {var subQ0=sQuery(id+"F25.wireOp",EDGE,"E60.top");Q1=makeQuery(id+"F25.imprint","IMPRINT",FACE,{"disambiguationData":[TD([[makeQuery(id+"F25.imprint","IMPRINT",EDGE,{"derivedFrom":subQ0}),-1.0]])]});}
            extrude(context, id + "F26", {"entities" : qUnion([Q0, Q1]), "oppositeDirection" : true, "depth" : 304.8 * mm, "offsetDistance" : 25.4 * mm});
        }
        {
            var Q0;
            {var subQ3=sQuery(id+"F25.wireOp",EDGE,"E62.bottom");Q0=makeQuery(id+"F25.imprint","IMPRINT",FACE,{"disambiguationData":[TD([[makeQuery(id+"F25.imprint","IMPRINT",EDGE,{"derivedFrom":subQ3}),1.0]])]});}
            var Q1;
            {var subQ3=sQuery(id+"F25.wireOp",EDGE,"E61.bottom");Q1=makeQuery(id+"F25.imprint","IMPRINT",FACE,{"disambiguationData":[TD([[makeQuery(id+"F25.imprint","IMPRINT",EDGE,{"derivedFrom":subQ3}),-1.0]])]});}
            extrude(context, id + "F27", {"entities" : qUnion([Q0, Q1]), "oppositeDirection" : true, "depth" : 304.8 * mm, "offsetDistance" : 25.4 * mm});
        }
        {
            var Q0;
            Q0 = qSketchRegion(id + "F8", true);
            extrude(context, id + "F28", {"entities" : qUnion([Q0]), "operationType" : NewBodyOperationType.REMOVE, "oppositeDirection" : true, "depth" : 841.25 * mm, "offsetDistance" : 25.4 * mm, "symmetric" : true});
        }
    });
